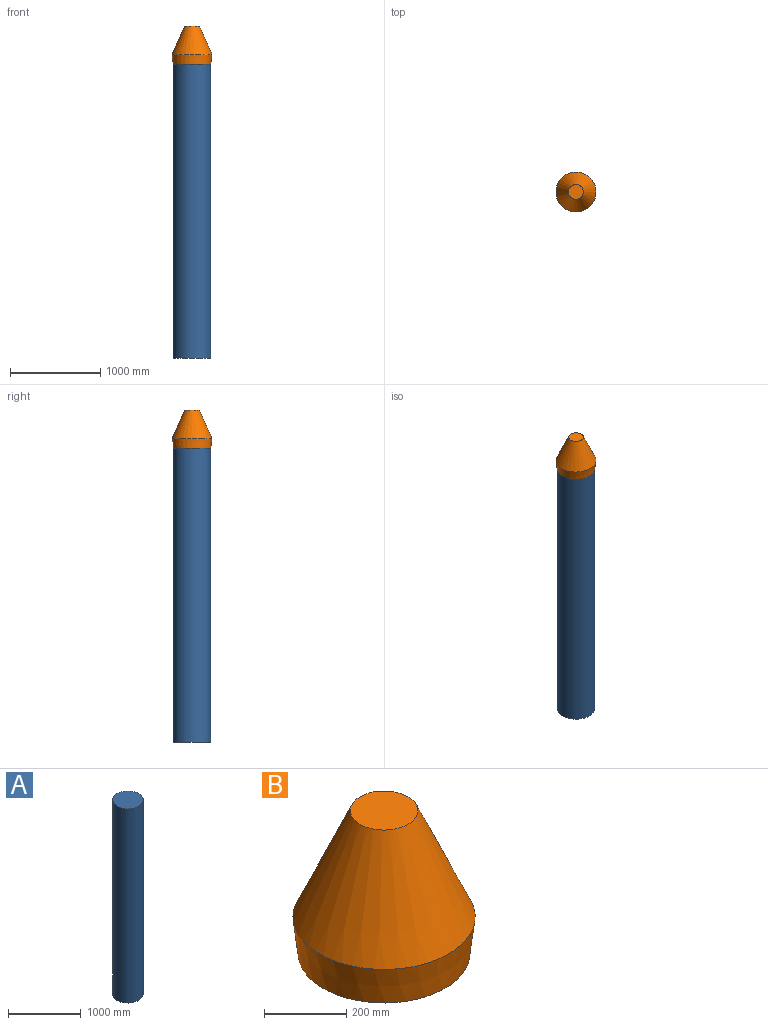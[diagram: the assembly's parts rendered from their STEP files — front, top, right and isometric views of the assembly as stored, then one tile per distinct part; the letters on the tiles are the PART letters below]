
ASSEMBLY  parts=2 mates=1
PART A: 3 faces, bbox 419.1x419.1x3261.4 mm
  f0: cylinder r=209.55mm len=3261.36mm, axis (0,0,-1), area 4294041.9mm2, adj f1,f2
  f1: plane 419.1x419.1mm, normal (0,0,1), area 137951.1mm2, adj f0
  f2: plane 419.1x419.1mm, normal (0,0,-1), area 137951.1mm2, adj f0
PART B: 4 faces, bbox 444.5x444.5x426.7 mm
  f0: cone r=82.55mm half-angle=23.7deg, axis (0,0,-1), area 332152.8mm2, adj f1,f3
  f1: cone r=222.25mm half-angle=6.6deg, axis (0,0,1), area 149159.5mm2, adj f0,f2
  f2: plane 419.1x419.1mm, normal (0,0,-1), area 137951.1mm2, adj f1
  f3: plane 165.1x165.1mm, normal (0,0,1), area 21408.4mm2, adj f0
PLACE A t=(40.59,14.46,-1664.23)mm
PLACE B t=(40.59,14.46,1706.35)mm
MATE fastened B.f0 <-> A.f0  axis (0,0,-1) through (40.59,14.46,1597.13)mm
